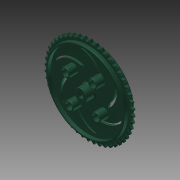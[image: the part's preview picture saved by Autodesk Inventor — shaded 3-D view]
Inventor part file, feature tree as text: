
AUTODESK INVENTOR PART (.ipt)
format: ipt  version: 2013 (Build 170138000, 138)  size: 3,502,080 bytes
history: native  units: mm (DEFAULTED — no unit token found)
features: imported_body x1, sketch x1, other x1, extrude x1
ambient origin geometry x8: Origin, YZ Plane, XZ Plane, XY Plane, X Axis, Y Axis, Z Axis, Center Point
bodies: Solid1 (feature_tree)
feature tree (4):
  imported_body  "Base1"
  sketch  "Sketch1"  dims[d1=2.2606mm d5=25.4mm d6=0.0mm d7=0.0mm d8=0.0mm]
  other  "Srf1"
  extrude  "ExtrusionSrf1"  Depth=25.4mm TaperAngle=0.0deg
